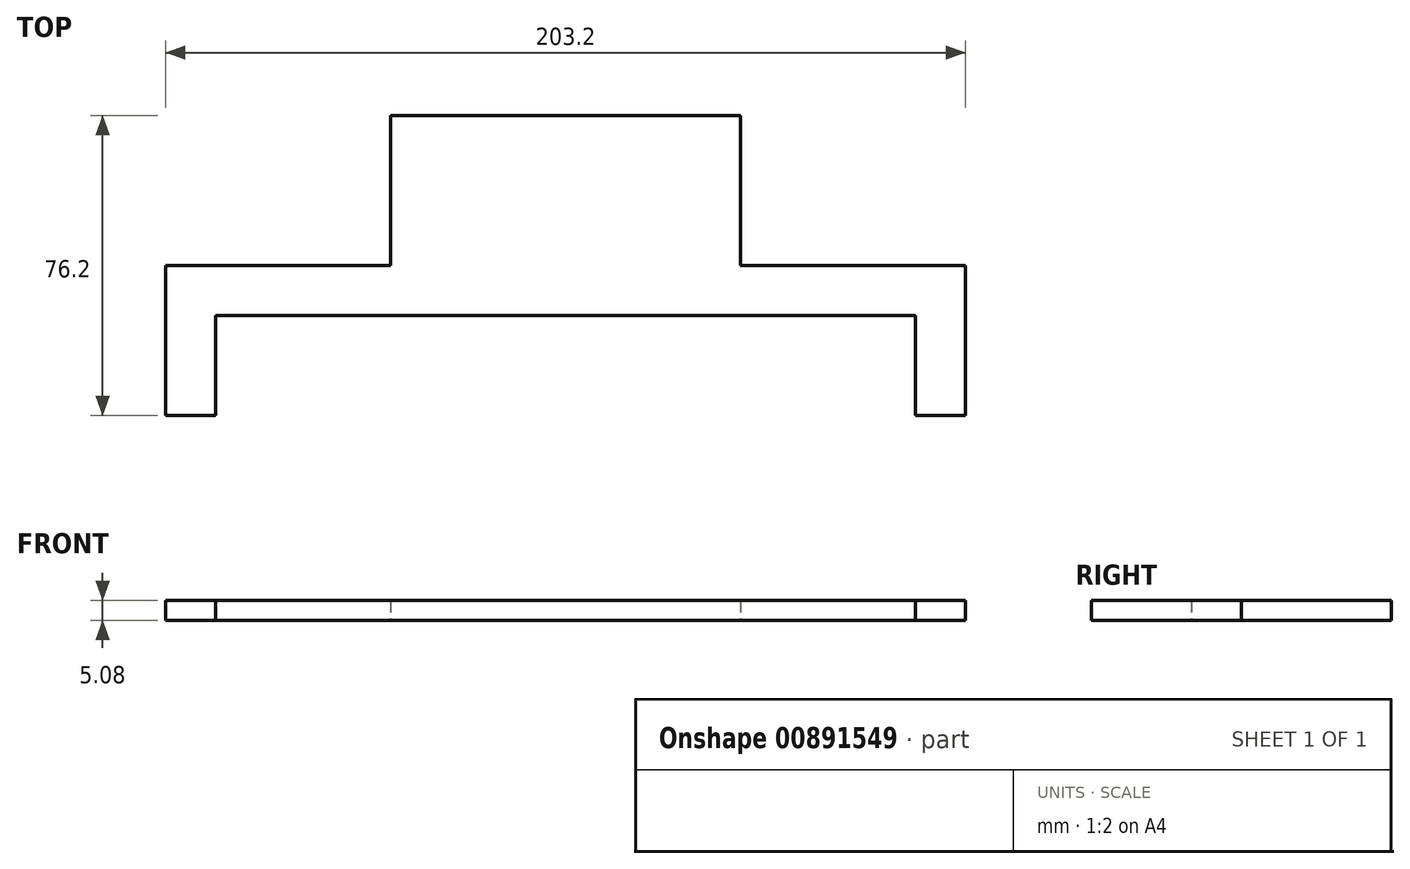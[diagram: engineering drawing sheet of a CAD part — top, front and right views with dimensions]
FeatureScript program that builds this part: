
annotation { "Feature Type Name" : "Feature", "Feature Type Description" : "" }
export const myFeature = defineFeature(function(context is Context, id is Id, definition is map)
    precondition{}
    {
        {
            var Q0;
            Q0=qCreatedBy(makeId("Top.planeOp"),FACE);
            var sketch = newSketch(context, id + "F0", { "sketchPlane" : qUnion([Q0])});
            skLineSegment(sketch, "E0", {"start": v(-45.89, -12.23) * mm, "end": v(-33.19, -12.23) * mm});
            skLineSegment(sketch, "E1", {"start": v(-33.19, -12.23) * mm, "end": v(-33.19, 13.17) * mm});
            skLineSegment(sketch, "E2", {"start": v(-33.19, 13.17) * mm, "end": v(144.61, 13.17) * mm});
            skLineSegment(sketch, "E3", {"start": v(144.61, 13.17) * mm, "end": v(144.61, -12.23) * mm});
            skLineSegment(sketch, "E4", {"start": v(144.61, -12.23) * mm, "end": v(157.31, -12.23) * mm});
            skLineSegment(sketch, "E5", {"start": v(157.31, -12.23) * mm, "end": v(157.31, 25.87) * mm});
            skLineSegment(sketch, "E6", {"start": v(157.31, 25.87) * mm, "end": v(100.16, 25.87) * mm});
            skLineSegment(sketch, "E7", {"start": v(100.16, 25.87) * mm, "end": v(100.16, 63.97) * mm});
            skLineSegment(sketch, "E8", {"start": v(100.16, 63.97) * mm, "end": v(11.26, 63.97) * mm});
            skLineSegment(sketch, "E9", {"start": v(11.26, 63.97) * mm, "end": v(11.26, 25.87) * mm});
            skLineSegment(sketch, "E10", {"start": v(-45.89, -12.23) * mm, "end": v(-45.89, 25.87) * mm});
            skLineSegment(sketch, "E11", {"start": v(-45.89, 25.87) * mm, "end": v(11.26, 25.87) * mm});
            skSolve(sketch);
        }
        {
            var Q0;
            Q0=makeQuery(id+"F0.imprint","IMPRINT",FACE,{"disambiguationData":[TD([[makeQuery(id+"F0.imprint","IMPRINT",EDGE,{"derivedFrom":sQuery(id+"F0.wireOp",EDGE,"E0")}),1.0]])]});
            extrude(context, id + "F1", {"entities" : qUnion([Q0]), "depth" : 5.08 * mm, "offsetDistance" : 25.4 * mm});
        }
    });
